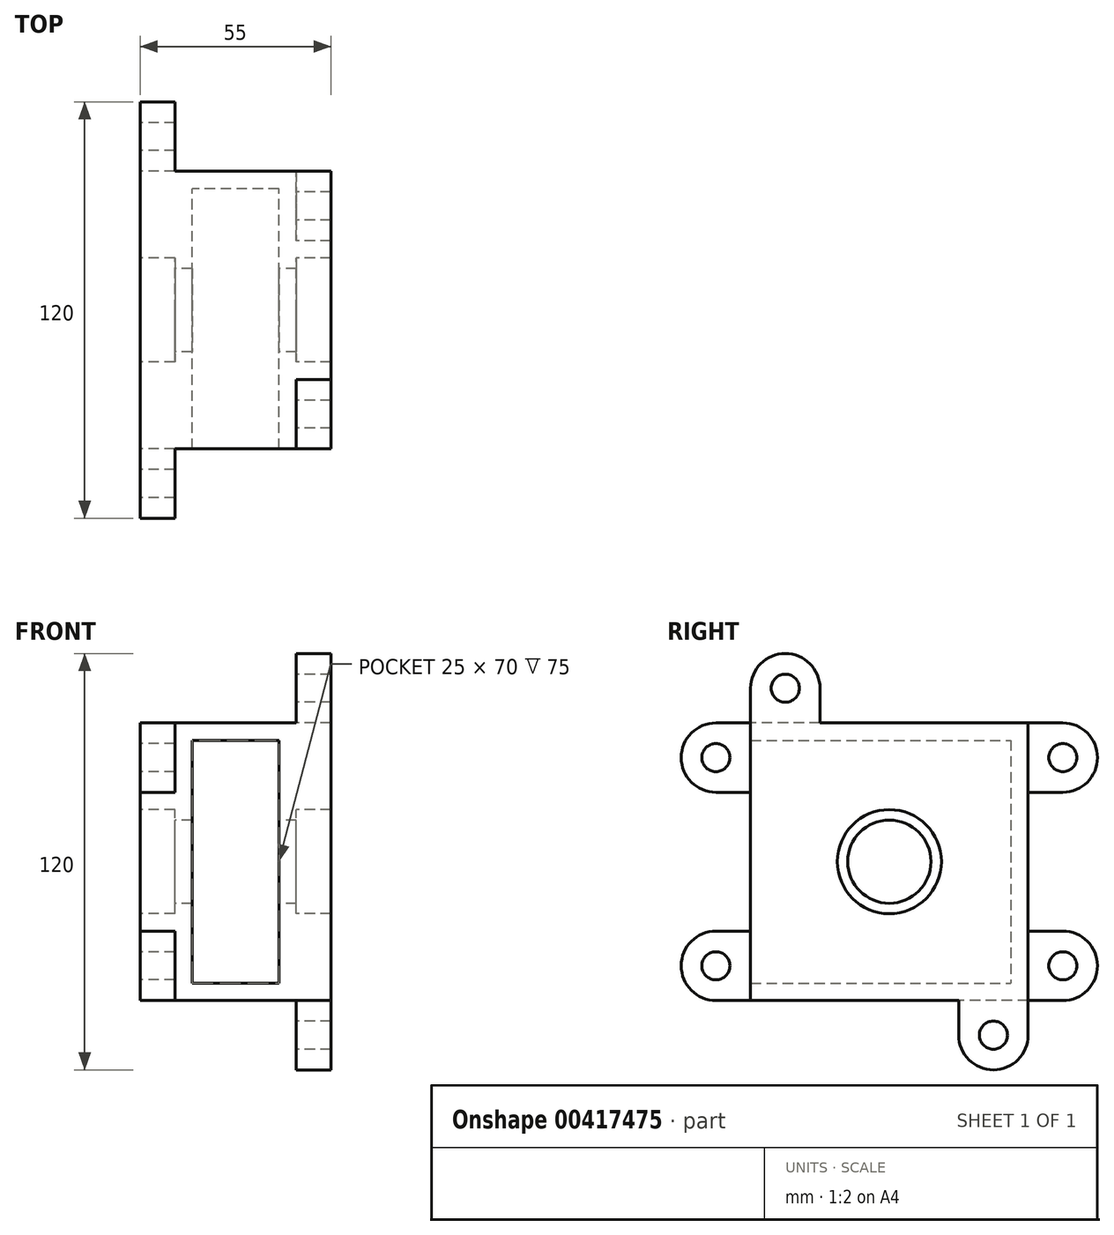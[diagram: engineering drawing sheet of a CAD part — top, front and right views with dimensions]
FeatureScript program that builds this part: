
annotation { "Feature Type Name" : "Feature", "Feature Type Description" : "" }
export const myFeature = defineFeature(function(context is Context, id is Id, definition is map)
    precondition{}
    {
        {
            var Q0;
            Q0=qCreatedBy(makeId("Right.planeOp"),FACE);
            var sketch = newSketch(context, id + "F0", { "sketchPlane" : qUnion([Q0])});
            skCircle(sketch, "E0", {"center": v(0, 0) * mm, "radius": 15 * mm});
            skCircle(sketch, "E1", {"center": v(0, 0) * mm, "radius": 12 * mm});
            skLineSegment(sketch, "E2.bottom", {"start": v(40, -40) * mm, "end": v(-40, -40) * mm});
            skLineSegment(sketch, "E2.top", {"start": v(40, 40) * mm, "end": v(-40, 40) * mm});
            skLineSegment(sketch, "E2.left", {"start": v(40, -40) * mm, "end": v(40, 40) * mm});
            skLineSegment(sketch, "E2.right", {"start": v(-40, -40) * mm, "end": v(-40, -35) * mm});
            skLineSegment(sketch, "E3.bottom", {"start": v(-40, 40) * mm, "end": v(40, 40) * mm});
            skLineSegment(sketch, "E3.top", {"start": v(-40, 35) * mm, "end": v(35, 35) * mm});
            skLineSegment(sketch, "E3.left", {"start": v(-40, 40) * mm, "end": v(-40, 35) * mm});
            skLineSegment(sketch, "E3.right", {"start": v(40, 40) * mm, "end": v(40, 35) * mm});
            skLineSegment(sketch, "E4.left", {"start": v(40, 35) * mm, "end": v(40, -40) * mm});
            skLineSegment(sketch, "E4.right", {"start": v(35, 35) * mm, "end": v(35, -35) * mm});
            skLineSegment(sketch, "E5.bottom", {"start": v(-40, -40) * mm, "end": v(35, -40) * mm});
            skLineSegment(sketch, "E5.top", {"start": v(-40, -35) * mm, "end": v(35, -35) * mm});
            skArc(sketch, "E6", {"start": v(-50, -20) * mm, "mid": v(-60, -30) * mm, "end": v(-50, -40) * mm});
            skLineSegment(sketch, "E7", {"start": v(-50, -20) * mm, "end": v(-40, -20) * mm});
            skLineSegment(sketch, "E8", {"start": v(-40, -40) * mm, "end": v(-50, -40) * mm});
            skCircle(sketch, "E9", {"center": v(-50, -30) * mm, "radius": 4.05 * mm});
            skArc(sketch, "E10", {"start": v(-50, 40) * mm, "mid": v(-60, 30) * mm, "end": v(-50, 20) * mm});
            skLineSegment(sketch, "E11", {"start": v(-50, -30) * mm, "end": v(-50, 48.78) * mm, "construction": true});
            skCircle(sketch, "E12", {"center": v(-50, 30) * mm, "radius": 4.05 * mm});
            skLineSegment(sketch, "E13", {"start": v(-50, 40) * mm, "end": v(-40, 40) * mm});
            skLineSegment(sketch, "E14", {"start": v(-50, 20) * mm, "end": v(-40, 20) * mm});
            skLineSegment(sketch, "E15.trimOffspring", {"start": v(-40, 35) * mm, "end": v(-40, 40) * mm});
            skLineSegment(sketch, "E16.trimOffspring", {"start": v(-40, -20) * mm, "end": v(-40, 20) * mm});
            skLineSegment(sketch, "E17", {"start": v(-40, 20) * mm, "end": v(-40, 35) * mm});
            skLineSegment(sketch, "E18", {"start": v(-40, -20) * mm, "end": v(-40, -35) * mm});
            skCircle(sketch, "E19", {"center": v(0, 0) * mm, "radius": 33.5 * mm, "construction": true});
            skLineSegment(sketch, "E20", {"start": v(-40, 40) * mm, "end": v(-40, 50) * mm});
            skLineSegment(sketch, "E21", {"start": v(-40, 50) * mm, "end": v(40, 50) * mm, "construction": true});
            skLineSegment(sketch, "E22", {"start": v(-40, 50) * mm, "end": v(-30, 50) * mm, "construction": true});
            skArc(sketch, "E23", {"start": v(-20, 50) * mm, "mid": v(-30, 60) * mm, "end": v(-40, 50) * mm});
            skLineSegment(sketch, "E24", {"start": v(-20, 50) * mm, "end": v(-20, 40) * mm});
            skLineSegment(sketch, "E25", {"start": v(-40, 50) * mm, "end": v(-40, 40) * mm});
            skCircle(sketch, "E26", {"center": v(-30, 50) * mm, "radius": 4.05 * mm});
            skArc(sketch, "E27", {"start": v(20, -50) * mm, "mid": v(30, -60) * mm, "end": v(40, -50) * mm});
            skLineSegment(sketch, "E28", {"start": v(40, -50) * mm, "end": v(40, -40) * mm});
            skLineSegment(sketch, "E29", {"start": v(20, -50) * mm, "end": v(20, -40) * mm});
            skCircle(sketch, "E30", {"center": v(30, -50) * mm, "radius": 4.05 * mm});
            skArc(sketch, "E31", {"start": v(50, 20) * mm, "mid": v(60, 30) * mm, "end": v(50, 40) * mm});
            skCircle(sketch, "E32", {"center": v(50, 30) * mm, "radius": 4.05 * mm});
            skLineSegment(sketch, "E33", {"start": v(50, 20) * mm, "end": v(40, 20) * mm});
            skLineSegment(sketch, "E34", {"start": v(50, 40) * mm, "end": v(40, 40) * mm});
            skLineSegment(sketch, "E35", {"start": v(40, 40) * mm, "end": v(40, 25) * mm});
            skArc(sketch, "E36", {"start": v(50, -40) * mm, "mid": v(60, -30) * mm, "end": v(50, -20) * mm});
            skCircle(sketch, "E37", {"center": v(50, -30) * mm, "radius": 4.05 * mm});
            skLineSegment(sketch, "E38", {"start": v(50, -40) * mm, "end": v(40, -40) * mm});
            skLineSegment(sketch, "E39", {"start": v(50, -20) * mm, "end": v(40, -20) * mm});
            skSolve(sketch);
        }
        {
            var Q0;
            Q0=makeQuery(id+"F0.imprint","IMPRINT",FACE,{"disambiguationData":[TD([[makeQuery(id+"F0.imprint","IMPRINT",EDGE,{"derivedFrom":sQuery(id+"F0.wireOp",EDGE,"E2.bottom")}),-1.0]])]});
            var Q1;
            Q1=makeQuery(id+"F0.imprint","IMPRINT",FACE,{"disambiguationData":[TD([[makeQuery(id+"F0.imprint","IMPRINT",EDGE,{"derivedFrom":sQuery(id+"F0.wireOp",EDGE,"E0")}),-1.0]])]});
            var Q2;
            Q2=makeQuery(id+"F0.imprint","IMPRINT",FACE,{"disambiguationData":[TD([[makeQuery(id+"F0.imprint","IMPRINT",EDGE,{"derivedFrom":sQuery(id+"F0.wireOp",EDGE,"E10")}),1.0]])]});
            var Q3;
            Q3=makeQuery(id+"F0.imprint","IMPRINT",FACE,{"disambiguationData":[TD([[makeQuery(id+"F0.imprint","IMPRINT",EDGE,{"derivedFrom":sQuery(id+"F0.wireOp",EDGE,"E2.right")}),1.0]])]});
            extrude(context, id + "F1", {"entities" : qUnion([Q0, Q1, Q2, Q3]), "depth" : 10 * mm});
        }
        {
            var Q0;
            Q0=makeQuery(id+"F0.imprint","IMPRINT",FACE,{"disambiguationData":[TD([[makeQuery(id+"F0.imprint","IMPRINT",EDGE,{"derivedFrom":sQuery(id+"F0.wireOp",EDGE,"E0")}),1.0]])]});
            var Q1;
            Q1=makeQuery(id+"F0.imprint","IMPRINT",FACE,{"disambiguationData":[TD([[makeQuery(id+"F0.imprint","IMPRINT",EDGE,{"derivedFrom":sQuery(id+"F0.wireOp",EDGE,"E0")}),-1.0]])]});
            var Q2;
            Q2=makeQuery(id+"F0.imprint","IMPRINT",FACE,{"disambiguationData":[TD([[makeQuery(id+"F0.imprint","IMPRINT",EDGE,{"derivedFrom":sQuery(id+"F0.wireOp",EDGE,"E2.bottom")}),-1.0]])]});
            extrude(context, id + "F2", {"entities" : qUnion([Q0, Q1, Q2]), "operationType" : NewBodyOperationType.ADD, "depth" : 15 * mm, "hasSecondDirection" : true, "secondDirectionOppositeDirection" : false, "secondDirectionDepth" : 10 * mm});
        }
        {
            var Q0;
            Q0=makeQuery(id+"F0.imprint","IMPRINT",FACE,{"disambiguationData":[TD([[makeQuery(id+"F0.imprint","IMPRINT",EDGE,{"derivedFrom":sQuery(id+"F0.wireOp",EDGE,"E2.bottom")}),-1.0]])]});
            extrude(context, id + "F3", {"entities" : qUnion([Q0]), "operationType" : NewBodyOperationType.ADD, "depth" : 40 * mm, "hasSecondDirection" : true, "secondDirectionOppositeDirection" : false, "secondDirectionDepth" : 15 * mm});
        }
        {
            var Q0;
            Q0=makeQuery(id+"F0.imprint","IMPRINT",FACE,{"disambiguationData":[TD([[makeQuery(id+"F0.imprint","IMPRINT",EDGE,{"derivedFrom":sQuery(id+"F0.wireOp",EDGE,"E2.bottom")}),-1.0]])]});
            var Q1;
            Q1=makeQuery(id+"F0.imprint","IMPRINT",FACE,{"disambiguationData":[TD([[makeQuery(id+"F0.imprint","IMPRINT",EDGE,{"derivedFrom":sQuery(id+"F0.wireOp",EDGE,"E0")}),-1.0]])]});
            var Q2;
            Q2=makeQuery(id+"F0.imprint","IMPRINT",FACE,{"disambiguationData":[TD([[makeQuery(id+"F0.imprint","IMPRINT",EDGE,{"derivedFrom":sQuery(id+"F0.wireOp",EDGE,"E0")}),1.0]])]});
            extrude(context, id + "F4", {"entities" : qUnion([Q0, Q1, Q2]), "operationType" : NewBodyOperationType.ADD, "depth" : 45 * mm, "hasSecondDirection" : true, "secondDirectionOppositeDirection" : false, "secondDirectionDepth" : 40 * mm});
        }
        {
            var Q0;
            Q0=makeQuery(id+"F0.imprint","IMPRINT",FACE,{"disambiguationData":[TD([[makeQuery(id+"F0.imprint","IMPRINT",EDGE,{"derivedFrom":sQuery(id+"F0.wireOp",EDGE,"E2.bottom")}),-1.0]])]});
            var Q1;
            Q1=makeQuery(id+"F0.imprint","IMPRINT",FACE,{"disambiguationData":[TD([[makeQuery(id+"F0.imprint","IMPRINT",EDGE,{"derivedFrom":sQuery(id+"F0.wireOp",EDGE,"E0")}),-1.0]])]});
            extrude(context, id + "F5", {"entities" : qUnion([Q0, Q1]), "operationType" : NewBodyOperationType.ADD, "depth" : 55 * mm, "hasSecondDirection" : true, "secondDirectionOppositeDirection" : false, "secondDirectionDepth" : 45 * mm});
        }
        {
            var Q0;
            Q0=makeQuery(id+"F0.imprint","IMPRINT",FACE,{"disambiguationData":[TD([[makeQuery(id+"F0.imprint","IMPRINT",EDGE,{"derivedFrom":sQuery(id+"F0.wireOp",EDGE,"E23")}),1.0]])]});
            var Q1;
            {var subQ1=sQuery(id+"F0.wireOp",EDGE,"E2.bottom");Q1=makeQuery(id+"F0.imprint","IMPRINT",FACE,{"disambiguationData":[TD([[makeQuery(id+"F0.imprint","IMPRINT",EDGE,{"derivedFrom":subQ1}),1.0]])]});}
            extrude(context, id + "F6", {"entities" : qUnion([Q0, Q1]), "operationType" : NewBodyOperationType.ADD, "depth" : 55 * mm, "hasSecondDirection" : true, "secondDirectionOppositeDirection" : false, "secondDirectionDepth" : 45 * mm});
        }
        {
            var Q0;
            Q0=makeQuery(id+"F0.imprint","IMPRINT",FACE,{"disambiguationData":[TD([[makeQuery(id+"F0.imprint","IMPRINT",EDGE,{"derivedFrom":sQuery(id+"F0.wireOp",EDGE,"E31")}),1.0]])]});
            var Q1;
            Q1=makeQuery(id+"F0.imprint","IMPRINT",FACE,{"disambiguationData":[TD([[makeQuery(id+"F0.imprint","IMPRINT",EDGE,{"derivedFrom":sQuery(id+"F0.wireOp",EDGE,"E36")}),1.0]])]});
            extrude(context, id + "F7", {"entities" : qUnion([Q0, Q1]), "operationType" : NewBodyOperationType.ADD, "depth" : 10 * mm});
        }
    });
